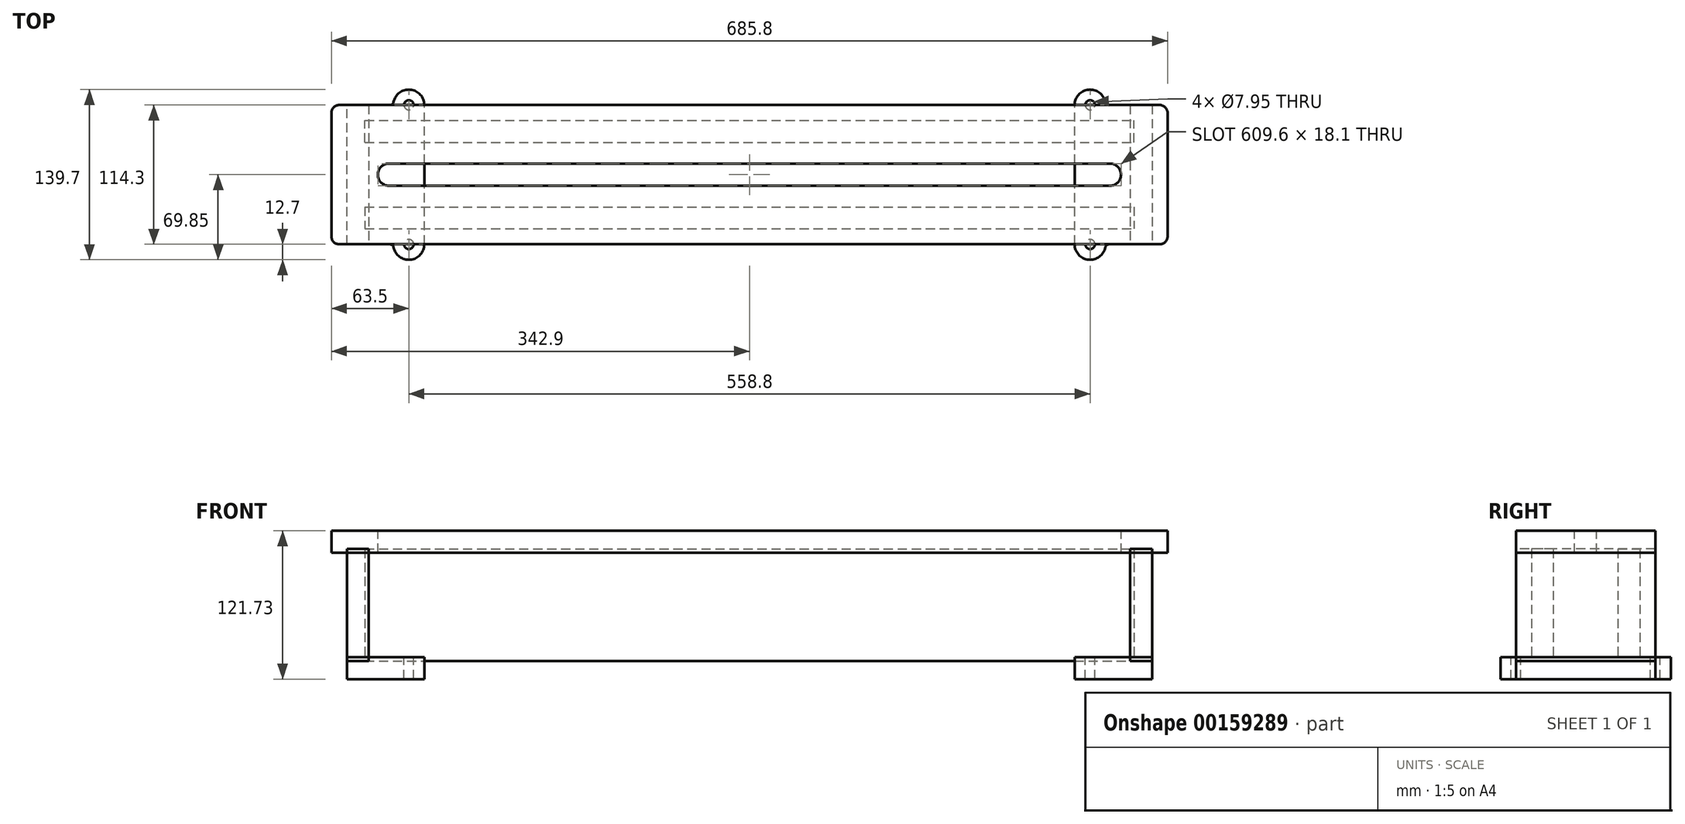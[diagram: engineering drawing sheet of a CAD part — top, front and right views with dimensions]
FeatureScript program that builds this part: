
annotation { "Feature Type Name" : "Feature", "Feature Type Description" : "" }
export const myFeature = defineFeature(function(context is Context, id is Id, definition is map)
    precondition{}
    {
        {
            var Q0;
            Q0=qCreatedBy(makeId("Top.planeOp"),FACE);
            var sketch = newSketch(context, id + "F0", { "sketchPlane" : qUnion([Q0])});
            skLineSegment(sketch, "E0.bottom", {"start": v(-342.9, -57.15) * mm, "end": v(342.9, -57.15) * mm});
            skLineSegment(sketch, "E0.top", {"start": v(-342.9, 57.15) * mm, "end": v(342.9, 57.15) * mm});
            skLineSegment(sketch, "E0.left", {"start": v(-342.9, -57.15) * mm, "end": v(-342.9, 57.15) * mm});
            skLineSegment(sketch, "E0.right", {"start": v(342.9, -57.15) * mm, "end": v(342.9, 57.15) * mm});
            skLineSegment(sketch, "E1", {"start": v(-342.9, -57.15) * mm, "end": v(342.9, 57.15) * mm, "construction": true});
            skSolve(sketch);
        }
        {
            assignVariable(context, id + "F1", {"name" : "Th", "anyValue" : 18 * mm});
        }
        {
            var Q0;
            Q0 = qSketchRegion(id + "F0", true);
            extrude(context, id + "F2", {"entities" : qUnion([Q0]), "depth" : getVariable(context, 'Th')});
        }
        {
            var Q0;
            Q0=makeQuery(id+"F2.opExtrude","CAP_FACE",FACE,{"disambiguationData":[OSD([sQuery(id+"F0.wireOp",EDGE,"E0.bottom"),sQuery(id+"F0.wireOp",EDGE,"E0.top"),sQuery(id+"F0.wireOp",EDGE,"E0.left"),sQuery(id+"F0.wireOp",EDGE,"E0.right")])],"isStart":false});
            var sketch = newSketch(context, id + "F3", { "sketchPlane" : qUnion([Q0])});
            skArc(sketch, "E2", {"start": v(-295.75, 9.05) * mm, "mid": v(-304.8, 0) * mm, "end": v(-295.75, -9.05) * mm});
            skArc(sketch, "E3", {"start": v(295.75, 9.05) * mm, "mid": v(304.8, 0) * mm, "end": v(295.75, -9.05) * mm});
            skLineSegment(sketch, "E4", {"start": v(-295.75, 9.05) * mm, "end": v(295.75, 9.05) * mm});
            skLineSegment(sketch, "E5", {"start": v(295.75, -9.05) * mm, "end": v(-295.75, -9.05) * mm});
            skSolve(sketch);
        }
        {
            var Q0;
            Q0 = qSketchRegion(id + "F3", true);
            extrude(context, id + "F4", {"entities" : qUnion([Q0]), "operationType" : NewBodyOperationType.REMOVE, "endBound" : BoundingType.THROUGH_ALL, "oppositeDirection" : true, "depth" : 25.4 * mm});
        }
        {
            var Q0;
            Q0=makeQuery(id+"F2.opExtrude","SWEPT_EDGE",EDGE,{"disambiguationData":[OSD([sQuery(id+"F0.wireOp",EDGE,"E0.bottom"),sQuery(id+"F0.wireOp",EDGE,"E0.left")])]});
            var Q1;
            Q1=makeQuery(id+"F2.opExtrude","SWEPT_EDGE",EDGE,{"disambiguationData":[OSD([sQuery(id+"F0.wireOp",EDGE,"E0.top"),sQuery(id+"F0.wireOp",EDGE,"E0.left")])]});
            var Q2;
            Q2=makeQuery(id+"F2.opExtrude","SWEPT_EDGE",EDGE,{"disambiguationData":[OSD([sQuery(id+"F0.wireOp",EDGE,"E0.top"),sQuery(id+"F0.wireOp",EDGE,"E0.right")])]});
            var Q3;
            Q3=makeQuery(id+"F2.opExtrude","SWEPT_EDGE",EDGE,{"disambiguationData":[OSD([sQuery(id+"F0.wireOp",EDGE,"E0.bottom"),sQuery(id+"F0.wireOp",EDGE,"E0.right")])]});
            fillet(context, id + "F5", {"entities" : qUnion([Q0, Q1, Q2, Q3]), "radius" : 6.35 * mm, "tangentPropagation" : true, "allowEdgeOverflow" : false});
        }
        {
            var Q0;
            Q0=makeQuery(id+"F2.opExtrude","SWEPT_FACE",FACE,{"disambiguationData":[OSD([sQuery(id+"F0.wireOp",EDGE,"E0.bottom")])]});
            var sketch = newSketch(context, id + "F6", { "sketchPlane" : qUnion([Q0])});
            skLineSegment(sketch, "E6.bottom", {"start": v(-330.2, -88.9) * mm, "end": v(-312.2, -88.9) * mm});
            skLineSegment(sketch, "E6.top", {"start": v(-330.2, 3.18) * mm, "end": v(-312.2, 3.18) * mm});
            skLineSegment(sketch, "E6.left", {"start": v(-330.2, -88.9) * mm, "end": v(-330.2, 3.17) * mm});
            skLineSegment(sketch, "E6.right", {"start": v(-312.2, -88.9) * mm, "end": v(-312.2, 3.17) * mm});
            skSolve(sketch);
        }
        {
            var Q0;
            Q0 = qSketchRegion(id + "F6", true);
            var Q1;
            Q1=makeQuery(id+"F2.opExtrude","SWEPT_FACE",FACE,{"disambiguationData":[OSD([sQuery(id+"F0.wireOp",EDGE,"E0.top")])]});
            extrude(context, id + "F7", {"entities" : qUnion([Q0]), "endBound" : BoundingType.UP_TO_SURFACE, "oppositeDirection" : true, "endBoundEntityFace" : qUnion([Q1]), "depth" : 25.4 * mm});
        }
        {
            var Q0;
            Q0=makeQuery(id+"F7.opExtrude","SWEPT_BODY",BODY,{"disambiguationData":[OSD([sQuery(id+"F6.wireOp",EDGE,"E6.bottom"),sQuery(id+"F6.wireOp",EDGE,"E6.top"),sQuery(id+"F6.wireOp",EDGE,"E6.left"),sQuery(id+"F6.wireOp",EDGE,"E6.right")])]});
            var Q1;
            Q1=qCreatedBy(makeId("Right.planeOp"),FACE);
            mirror(context, id + "F8", {"entities" : qUnion([Q0]), "mirrorPlane" : qUnion([Q1])});
        }
        {
            var Q0;
            Q0=makeQuery(id+"F2.opExtrude","SWEPT_FACE",FACE,{"disambiguationData":[OSD([sQuery(id+"F0.wireOp",EDGE,"E0.bottom")])]});
            cPlane(context, id + "F9", {"entities" : qUnion([Q0]), "cplaneType" : CPlaneType.OFFSET, "offset" : 12.7 * mm, "oppositeDirection" : true, "width" : 152.4 * mm, "height" : 152.4 * mm});
        }
        {
            var Q0;
            Q0=qCreatedBy(id+"F9.planeOp",FACE);
            var sketch = newSketch(context, id + "F10", { "sketchPlane" : qUnion([Q0])});
            skLineSegment(sketch, "E7.bottom", {"start": v(-315.38, 3.17) * mm, "end": v(315.38, 3.17) * mm});
            skLineSegment(sketch, "E7.top", {"start": v(-315.38, -88.9) * mm, "end": v(315.38, -88.9) * mm});
            skLineSegment(sketch, "E7.left", {"start": v(-315.38, 3.17) * mm, "end": v(-315.38, -88.9) * mm});
            skLineSegment(sketch, "E7.right", {"start": v(315.38, 3.18) * mm, "end": v(315.38, -88.9) * mm});
            skSolve(sketch);
        }
        {
            var Q0;
            Q0 = qSketchRegion(id + "F10", true);
            extrude(context, id + "F11", {"entities" : qUnion([Q0]), "oppositeDirection" : true, "depth" : getVariable(context, 'Th')});
        }
        {
            var Q0;
            Q0=makeQuery(id+"F11.opExtrude","SWEPT_BODY",BODY,{"disambiguationData":[OSD([sQuery(id+"F10.wireOp",EDGE,"E7.bottom"),sQuery(id+"F10.wireOp",EDGE,"E7.top"),sQuery(id+"F10.wireOp",EDGE,"E7.left"),sQuery(id+"F10.wireOp",EDGE,"E7.right")])]});
            var Q1;
            Q1=qCreatedBy(makeId("Front.planeOp"),FACE);
            mirror(context, id + "F12", {"entities" : qUnion([Q0]), "mirrorPlane" : qUnion([Q1])});
        }
        {
            var Q0;
            Q0=makeQuery(id+"F7.opExtrude","SWEPT_FACE",FACE,{"disambiguationData":[OSD([sQuery(id+"F6.wireOp",EDGE,"E6.bottom")])]});
            cPlane(context, id + "F13", {"entities" : qUnion([Q0]), "cplaneType" : CPlaneType.OFFSET, "offset" : 3.17 * mm, "oppositeDirection" : true, "width" : 152.4 * mm, "height" : 152.4 * mm});
        }
        {
            var Q0;
            Q0=qCreatedBy(id+"F13.planeOp",FACE);
            var sketch = newSketch(context, id + "F14", { "sketchPlane" : qUnion([Q0])});
            skLineSegment(sketch, "E8", {"start": v(-330.2, 57.15) * mm, "end": v(-330.2, -57.15) * mm});
            skLineSegment(sketch, "E9", {"start": v(-330.2, -57.15) * mm, "end": v(-294.95, -57.15) * mm});
            skLineSegment(sketch, "E10", {"start": v(-330.2, 57.15) * mm, "end": v(-294.95, 57.15) * mm});
            skArc(sketch, "E11", {"start": v(-291.84, 59.69) * mm, "mid": v(-278.12, 69.79) * mm, "end": v(-266.7, 57.15) * mm});
            skArc(sketch, "E12", {"start": v(-291.84, -59.69) * mm, "mid": v(-278.12, -69.79) * mm, "end": v(-266.7, -57.15) * mm});
            skLineSegment(sketch, "E13", {"start": v(-266.7, 57.15) * mm, "end": v(-266.7, -57.15) * mm});
            skCircle(sketch, "E14", {"center": v(-279.4, 57.15) * mm, "radius": 3.98 * mm});
            skCircle(sketch, "E15", {"center": v(-279.4, -57.15) * mm, "radius": 3.98 * mm});
            skPoint(sketch, "E16.visualSharp", {"position": v(-292.1, -57.15) * mm});
            skArc(sketch, "E16.filletArc", {"start": v(-291.84, -59.69) * mm, "mid": v(-292.95, -57.87) * mm, "end": v(-294.95, -57.15) * mm});
            skPoint(sketch, "E17.visualSharp", {"position": v(-292.1, 57.15) * mm});
            skArc(sketch, "E17.filletArc", {"start": v(-294.95, 57.15) * mm, "mid": v(-292.95, 57.87) * mm, "end": v(-291.84, 59.69) * mm});
            skSolve(sketch);
        }
        {
            var Q0;
            Q0 = qSketchRegion(id + "F14", true);
            extrude(context, id + "F15", {"entities" : qUnion([Q0]), "depth" : getVariable(context, 'Th')});
        }
        {
            var Q0;
            Q0=makeQuery(id+"F15.opExtrude","SWEPT_BODY",BODY,{"disambiguationData":[OSD([sQuery(id+"F14.wireOp",EDGE,"E8"),sQuery(id+"F14.wireOp",EDGE,"E9"),sQuery(id+"F14.wireOp",EDGE,"E10"),sQuery(id+"F14.wireOp",EDGE,"E11"),sQuery(id+"F14.wireOp",EDGE,"E12"),sQuery(id+"F14.wireOp",EDGE,"E13"),sQuery(id+"F14.wireOp",EDGE,"E14"),sQuery(id+"F14.wireOp",EDGE,"E15"),sQuery(id+"F14.wireOp",EDGE,"E16.filletArc"),sQuery(id+"F14.wireOp",EDGE,"E17.filletArc")])]});
            var Q1;
            Q1=qCreatedBy(makeId("Right.planeOp"),FACE);
            mirror(context, id + "F16", {"entities" : qUnion([Q0]), "mirrorPlane" : qUnion([Q1])});
        }
    });
